# Revit family: FOR UPDATE_26052USA_NEW
name_source: partatom
category: Plumbing Fixtures
revit_build: Autodesk Revit 2018 (Build: 20170223_1515(x64)
units: mm (PartAtom-declared; Revit-internal decimal feet)

## family parameters
Always vertical = No
Cut with Voids When Loaded = No
OmniClass Number = 23.31.17.00
OmniClass Title = Showers
Part Type = Normal
Room Calculation Point = No
Round Connector Dimension = Use Diameter
Shared = No
Work Plane-Based = Yes

## types (6) — shared parameters
Always visible = Yes
BIMobject category = Showers
Default Elevation = 1219.2 mm  [stored 4 ft]
Description = AXOR ShowerSolutions Hand shower 120 3jet 1.75 GPM
Design country = Germany
EAN code = 4059625405093
Edition number = 1
IFC Classification = Sanitary Terminal
Manufacturer = AXOR
Manufacturer country = Germany
Manufacturer name = AXOR
Material main = Plastic
Material secondary = Chrome
Model = 26052USA
OmniClass Code = 23-31 17 00
OmniClass Description = Showers
Product Guid = 8fbe5139-5ae7-4600-b450-2fd96c03f7ee
Product SKU = 26052USA
Product data url = https://bimobject.com
Product family = AXOR ShowerSolutions
Product group = Hand showers
Product name = 26052USA AXOR ShowerSolutions Hand shower 120 3jet 1.75 GPM
QR code = https://bimobject.com
URL = https://www.axor-design.com
Water Inlet = 13 mm
Water Inlet Description = Water Inlet 12.7mm
Weight Net (Kg) = 265

## per-type parameters (varying)
| type | Material 1 |
| 001 Chrome | AXOR - Metal - 001 Chrome |
| 141 Brushed Bronze | AXOR - Metal - 141 Brushed Bronze |
| 331 Polished Black Chrome | AXOR - Metal - 331 Polished Black Chrome |
| 671 Matt Black | AXOR - Metal - 671 Matt Black |
| 821 Brushed Nickel | AXOR - Metal - 821 Brushed Nickel |
| 991 Polished Gold Optic | AXOR - Metal - 991 Polished Gold Optic |

note: [stored X ft] marks values corroborated as IEEE doubles in the binary element streams (Revit-internal decimal feet)
